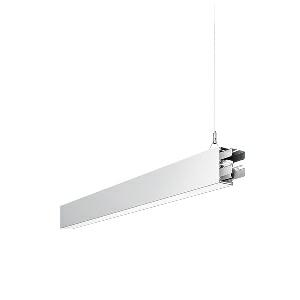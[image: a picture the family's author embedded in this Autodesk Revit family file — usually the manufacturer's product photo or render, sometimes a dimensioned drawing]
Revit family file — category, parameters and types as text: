
# Revit family: dotoo_line_-_dlp_1500_830_d_mid_00805803_1699
name_source: partatom
category: Lighting Fixtures
units: mm (PartAtom-declared; Revit-internal decimal feet)

## family parameters
Cut with Voids When Loaded = No
Host = Face
Light Source = No
Part Type = Normal
Room Calculation Point = No
Round Connector Dimension = Use Diameter
Shared = No

## types (1)
- DOTOO.line - DLP 1500/830/D MID (1 x LED, 1300 lm, 3000K)
    Apparent Load = 13 VA
    Approval mark = CE
    CIE Flux Codes = 67 91 98 100 100
    Color Rendering = 80-89
    Color Temperature = 3000K
    Control Gear = Electronic ballast
    Default Elevation = 1800 mm
    Description = DLP 1500/830/D|Suspended luminaire|light source: LED|connected load: 220-240 V, 50/60 Hz|Power consumption: approx. 13 W|standby: approx. 0,20|luminous flux: 1300 lm|luminous efficacy: 100 lm/W|light distribution: Direct|direct ratio: approx. 100 %|colour temperature: Warm white, ca. 3000 K|color rendering index (CRI): >= 80|chromaticity tolerance:  3 SDCM|System of protection: IP 40|technology: Continuously dimmable|luminaire body|material: Sectional aluminium|colour: White|lamp cover: Acrylic (PMMA), Clear|mains lead: 1,0 m With free stranded wires|Fastening: Steel cable 0.3 - 0.7 m|glare control: Prism aperture|luminance(L65): <= 3000 cd/m|unified glare rating(4H 8H): <=  19|special features: DALI Load 1x, TouchDIM - dimming via standard switch, Through-wired, up to 18 m on one mains connection, Flicker-free, Suitable as emergency lighting, Mechanical and electrical connection of the individual modules without tools|
    Frequency = 50 Hz
    Height = 110 mm
    Lamp = 1 x LED
    Lamp Light Flux = 1300 lm
    Lamp count = 1
    Length = 1122 mm
    Luminous efficacy = 100 lm/W
    Manufacturer = Waldmann
    ModVariant = No
    Model = 00805803
    Mounting Place = Ceiling
    Mounting Type = Pendant
    Number of Poles = 1
    OnlyDefault = Yes
    Power Factor = 1
    Product Name = DOTOO.line - DLP 1500/830/D MID
    Product group = Suspended luminaire
    ProductGroupID = 9
    Protection Class = Protection class I
    Protection Degree = IP 40
    RLX_Detail_Level = 1
    RLX_Emergency_Light_Flux = 0 lm
    RLX_Emergency_Type = 0
    RLX_Emergency_Type_DB = No
    RlxData = <blob elided: 19465 chars, md5=dbb21273>
    Socket = socket
    Standby Power = 0 W
    System Light Flux = 1300 lm
    System Power = 13 W
    Type Comments = Product without accessories
    Type Image = 113302000-00692570.jpg
    URL = http://relux.com
    VarID = ---
    Voltage = 230 V
    Voltage Range = 220-240 V
    Weight = 0.00 kg
    Width = 60 mm  [stored 0.19685 ft]

note: [stored X ft] marks values corroborated as IEEE doubles in the binary element streams (Revit-internal decimal feet)

## geometry (parser evidence)
native form markers: Blend x4, Sweep x12
no freeform markers — native parametric forms only
